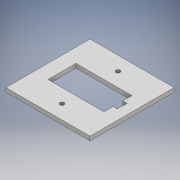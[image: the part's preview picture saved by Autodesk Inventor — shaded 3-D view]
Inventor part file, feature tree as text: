
AUTODESK INVENTOR PART (.ipt)
format: ipt  version: 2017 (Build 210142000, 142)  size: 111,104 bytes
history: native  units: mm
features: extrude x1, sketch x1
ambient origin geometry x8: Origin, YZ Plane, XZ Plane, XY Plane, X Axis, Y Axis, Z Axis, Center Point
bodies: Body1 (feature_tree)
feature tree (2):
  extrude  "Extrusion2"  Depth=20.0mm
  sketch  "Sketch1"  dims[d0=40.0mm d1=20.0mm d2=60.0mm d3=60.0mm d4=10.0mm d5=10.0mm d6=3.0mm d7=3.0mm d11=7.0mm d12=3.0mm d13=0.0mm]
